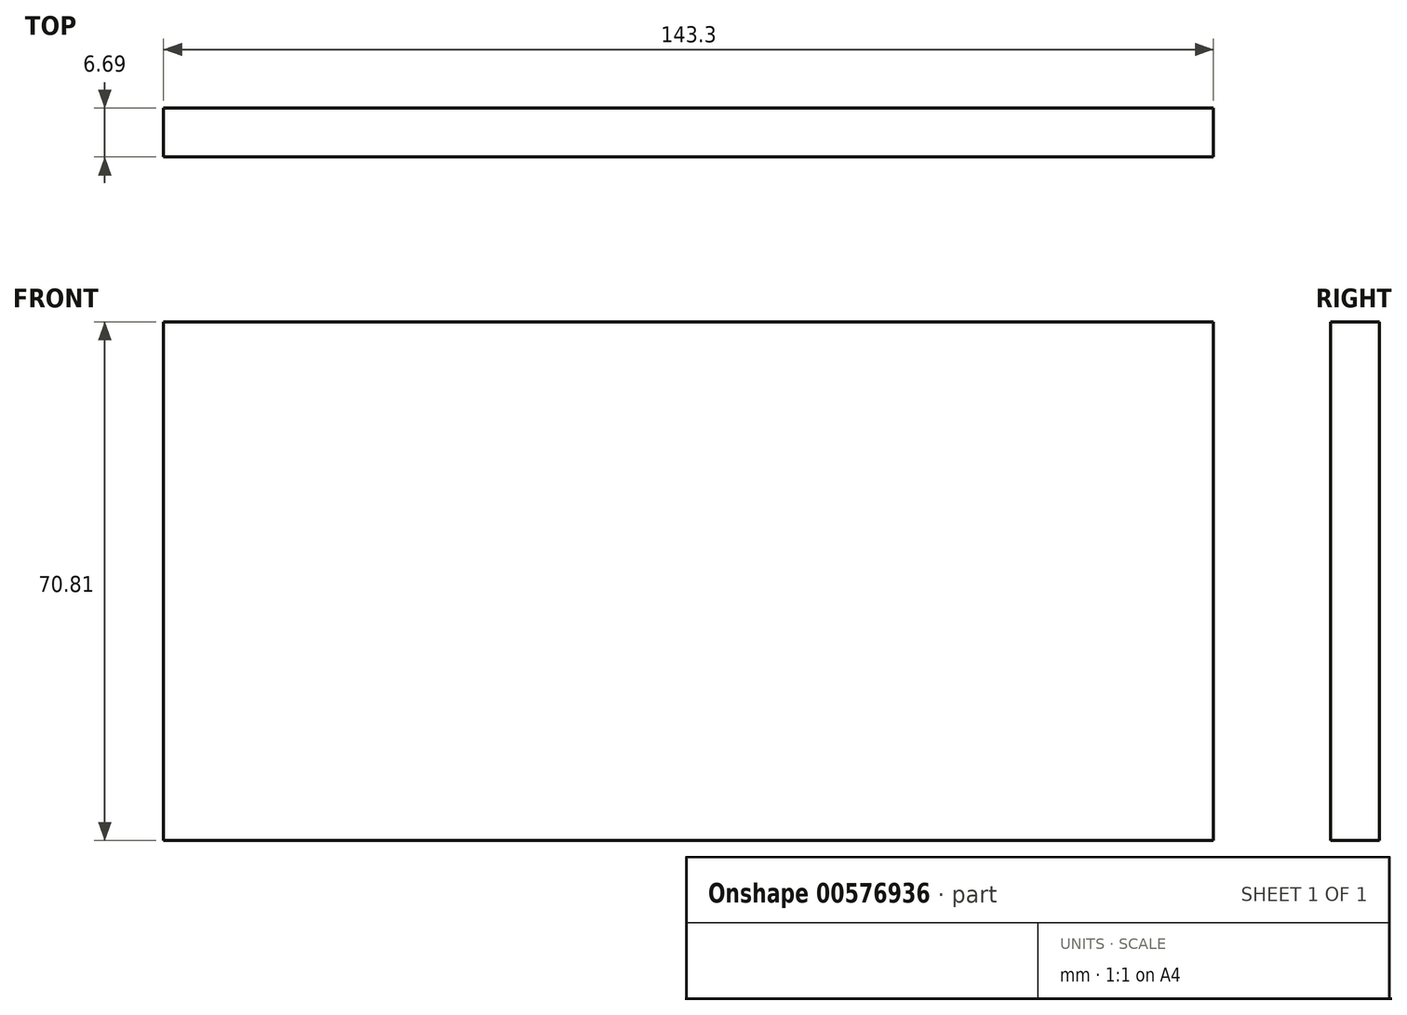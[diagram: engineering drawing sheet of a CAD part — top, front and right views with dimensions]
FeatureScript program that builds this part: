
annotation { "Feature Type Name" : "Feature", "Feature Type Description" : "" }
export const myFeature = defineFeature(function(context is Context, id is Id, definition is map)
    precondition{}
    {
        {
            var Q0;
            Q0=qCreatedBy(makeId("Front.planeOp"),FACE);
            var sketch = newSketch(context, id + "F0", { "sketchPlane" : qUnion([Q0])});
            skLineSegment(sketch, "E0.bottom", {"start": v(-88.32, 22.63) * mm, "end": v(54.98, 22.63) * mm});
            skLineSegment(sketch, "E0.top", {"start": v(-88.32, -48.18) * mm, "end": v(54.98, -48.18) * mm});
            skLineSegment(sketch, "E0.left", {"start": v(-88.32, 22.63) * mm, "end": v(-88.32, -48.18) * mm});
            skLineSegment(sketch, "E0.right", {"start": v(54.98, 22.63) * mm, "end": v(54.98, -48.18) * mm});
            skSolve(sketch);
        }
        {
            var Q0;
            Q0 = qSketchRegion(id + "F0", true);
            extrude(context, id + "F1", {"entities" : qUnion([Q0]), "depth" : 6.7 * mm, "offsetDistance" : 25 * mm});
        }
    });
